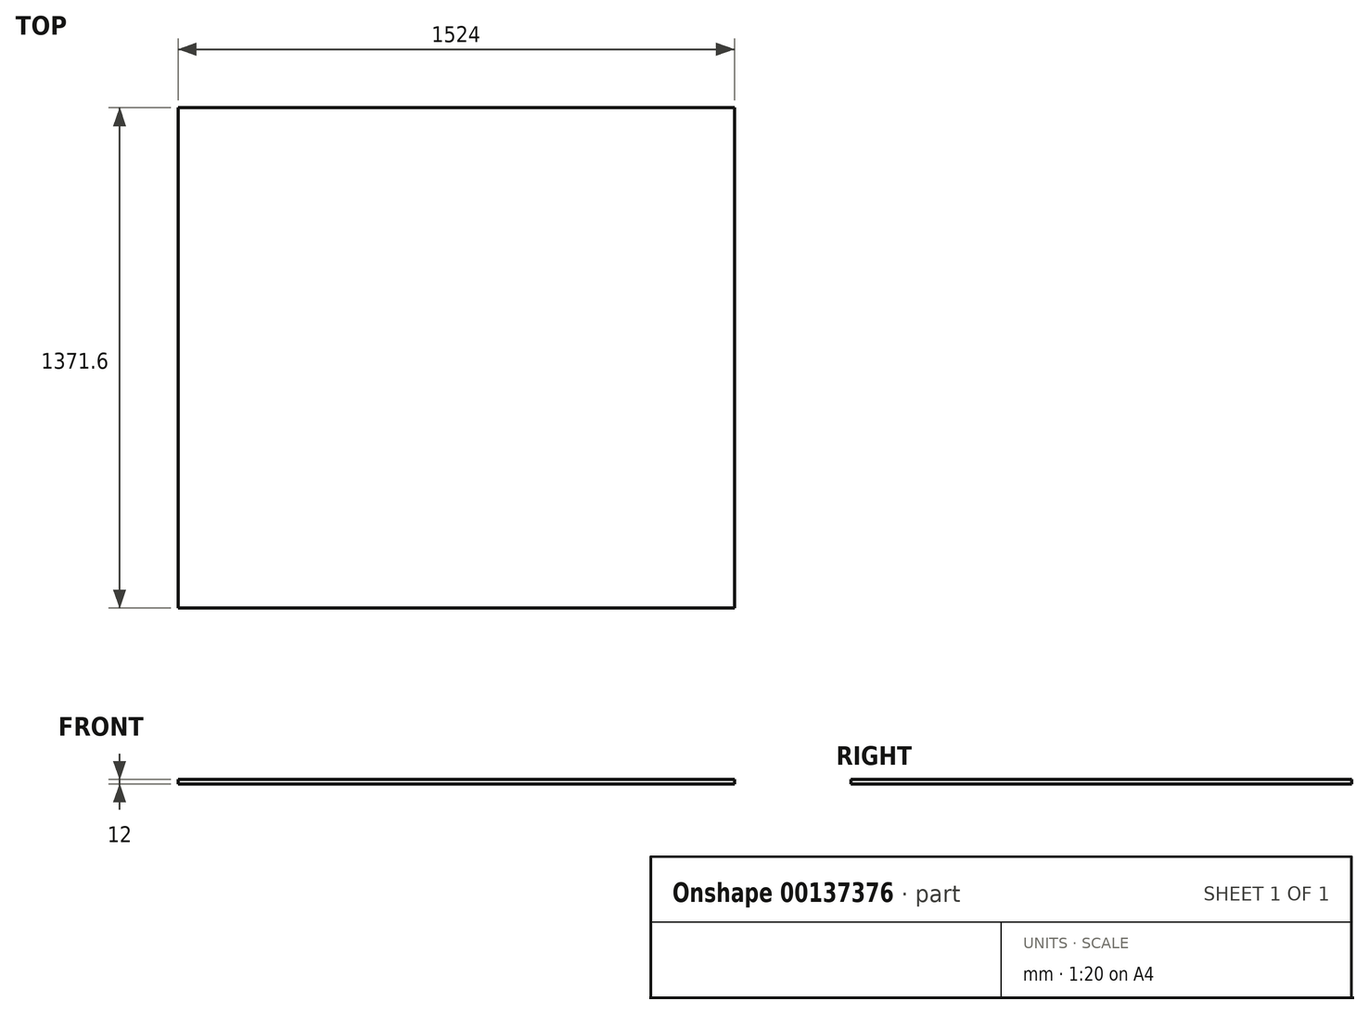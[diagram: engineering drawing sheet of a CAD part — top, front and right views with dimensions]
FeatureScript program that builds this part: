
annotation { "Feature Type Name" : "Feature", "Feature Type Description" : "" }
export const myFeature = defineFeature(function(context is Context, id is Id, definition is map)
    precondition{}
    {
        {
            var Q0;
            Q0=qCreatedBy(makeId("Top.planeOp"),FACE);
            var sketch = newSketch(context, id + "F0", { "sketchPlane" : qUnion([Q0])});
            skLineSegment(sketch, "E0.bottom", {"start": v(-731.5, -677.83) * mm, "end": v(792.5, -677.83) * mm});
            skLineSegment(sketch, "E0.top", {"start": v(-731.5, 693.77) * mm, "end": v(792.5, 693.77) * mm});
            skLineSegment(sketch, "E0.left", {"start": v(-731.5, -677.83) * mm, "end": v(-731.5, 693.77) * mm});
            skLineSegment(sketch, "E0.right", {"start": v(792.5, -677.83) * mm, "end": v(792.5, 693.77) * mm});
            skSolve(sketch);
        }
        {
            var Q0;
            Q0 = qSketchRegion(id + "F0", true);
            var Q1;
            Q1=makeQuery(id+"F0.imprint","IMPRINT",FACE,{"disambiguationData":[TD([[makeQuery(id+"F0.imprint","IMPRINT",EDGE,{"derivedFrom":sQuery(id+"F0.wireOp",EDGE,"E0.bottom")}),1.0]])]});
            extrude(context, id + "F1", {"entities" : qUnion([Q0, Q1]), "depth" : 12 * mm});
        }
    });
